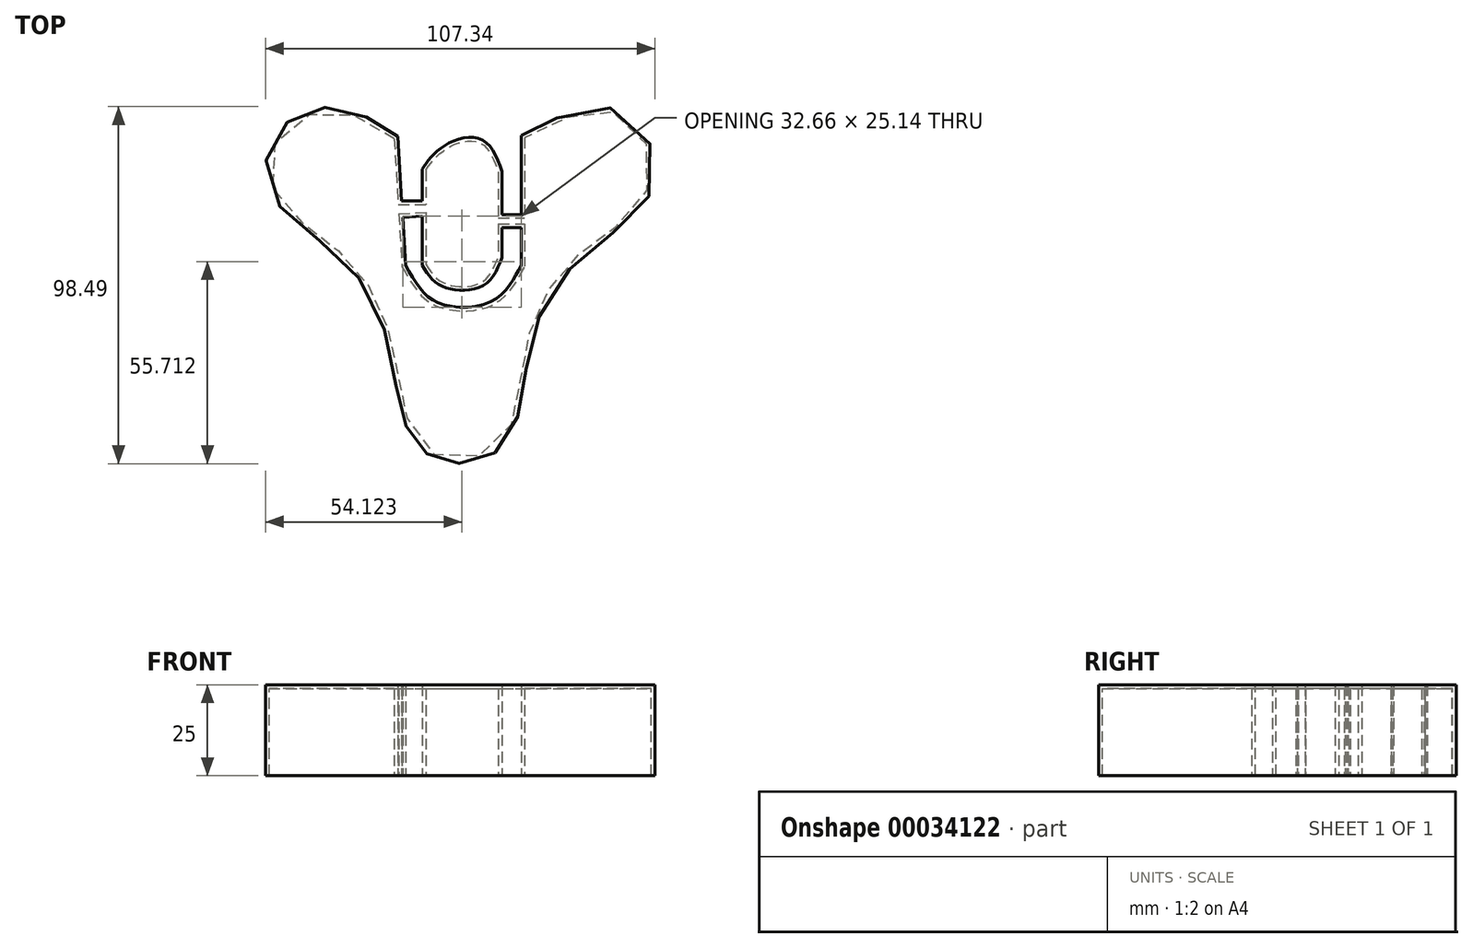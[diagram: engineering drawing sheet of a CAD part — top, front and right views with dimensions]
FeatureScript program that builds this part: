
annotation { "Feature Type Name" : "Feature", "Feature Type Description" : "" }
export const myFeature = defineFeature(function(context is Context, id is Id, definition is map)
    precondition{}
    {
        {
            var Q0;
            Q0=qCreatedBy(makeId("Top.planeOp"),FACE);
            var sketch = newSketch(context, id + "F0", { "sketchPlane" : qUnion([Q0])});
            skLineSegment(sketch, "E0", {"start": v(-18.13, 47.47) * mm, "end": v(-15.97, 11.9) * mm});
            skLineSegment(sketch, "E1", {"start": v(15.88, 47.77) * mm, "end": v(15.88, 11.9) * mm});
            skLineSegment(sketch, "E2", {"start": v(-11.33, 38.5) * mm, "end": v(-11.33, 11.9) * mm});
            skLineSegment(sketch, "E3", {"start": v(10.63, 37.88) * mm, "end": v(10.63, 14.07) * mm});
            skLineSegment(sketch, "E4", {"start": v(-17.05, 29.68) * mm, "end": v(-11.33, 29.68) * mm});
            skLineSegment(sketch, "E5", {"start": v(-16.78, 25.2) * mm, "end": v(-11.33, 25.53) * mm});
            skPoint(sketch, "E5.startSnap0", {"position": v(-11.33, 25.2) * mm});
            skLineSegment(sketch, "E6", {"start": v(10.63, 25.97) * mm, "end": v(15.88, 25.97) * mm});
            skLineSegment(sketch, "E7", {"start": v(10.63, 22.42) * mm, "end": v(15.88, 22.42) * mm});
            skFitSpline(sketch, "E8", {"points": [v(-18.13, 47.47) * mm, v(-24.32, 51.48) * mm, v(-34.52, 55.5) * mm, v(-44.72, 53.65) * mm, v(-52.15, 47.47) * mm, v(-54, 34.17) * mm, v(-44.42, 22.42) * mm, v(-31.12, 11.29) * mm, v(-21.84, -5.72) * mm, v(-18.13, -23.96) * mm, v(-15.66, -32.93) * mm, v(-11.64, -38.8) * mm, v(-4.84, -42.52) * mm, v(1.66, -42.2) * mm, v(10, -38.8) * mm, v(15.26, -28.6) * mm, v(17.74, -13.45) * mm, v(23.3, 2.94) * mm, v(36.3, 17.47) * mm, v(49.28, 27.98) * mm, v(52.06, 43.75) * mm, v(40, 55.5) * mm, v(23.3, 51.48) * mm, v(15.88, 47.77) * mm], "startDerivative": vector(-171.76, 118.34) * mm, "endDerivative": vector(-183.23, -94.5) * mm});
            skFitSpline(sketch, "E9", {"points": [v(-11.33, 38.5) * mm, v(-8.55, 42.2) * mm, v(-2.05, 46.54) * mm, v(5.68, 46.23) * mm, v(10.63, 37.88) * mm], "startDerivative": vector(11.88, 18.4) * mm, "endDerivative": vector(13.45, -35.6) * mm});
            skFitSpline(sketch, "E10", {"points": [v(-11.33, 11.9) * mm, v(-7.62, 7.27) * mm, v(-1.43, 5.1) * mm, v(6.3, 6.96) * mm, v(10.63, 14.07) * mm], "startDerivative": vector(14.25, -22.57) * mm, "endDerivative": vector(12.37, 30.63) * mm});
            skFitSpline(sketch, "E11", {"points": [v(-15.97, 11.9) * mm, v(-11.33, 4.8) * mm, v(-5.45, 1.08) * mm, v(6.3, 1.4) * mm, v(12.8, 6.65) * mm, v(15.88, 11.9) * mm], "startDerivative": vector(21.66, -38.15) * mm, "endDerivative": vector(15.75, 30.42) * mm});
            skSolve(sketch);
        }
        {
            var Q0;
            Q0 = qSketchRegion(id + "F0", true);
            extrude(context, id + "F1", {"entities" : qUnion([Q0]), "depth" : 25 * mm});
        }
        {
            var Q0;
            Q0=makeQuery(id+"F1.opExtrude","CAP_FACE",FACE,{"disambiguationData":[OSD([sQuery(id+"F0.wireOp",EDGE,"E0"),sQuery(id+"F0.wireOp",EDGE,"E1"),sQuery(id+"F0.wireOp",EDGE,"E2"),sQuery(id+"F0.wireOp",EDGE,"E3"),sQuery(id+"F0.wireOp",EDGE,"E4"),sQuery(id+"F0.wireOp",EDGE,"E5"),sQuery(id+"F0.wireOp",EDGE,"E6"),sQuery(id+"F0.wireOp",EDGE,"E7"),sQuery(id+"F0.wireOp",EDGE,"E8"),sQuery(id+"F0.wireOp",EDGE,"E9"),sQuery(id+"F0.wireOp",EDGE,"E10"),sQuery(id+"F0.wireOp",EDGE,"E11")])],"isStart":true});
            shell(context, id + "F2", {"entities" : qUnion([Q0]), "thickness" : 1 * mm});
        }
    });
